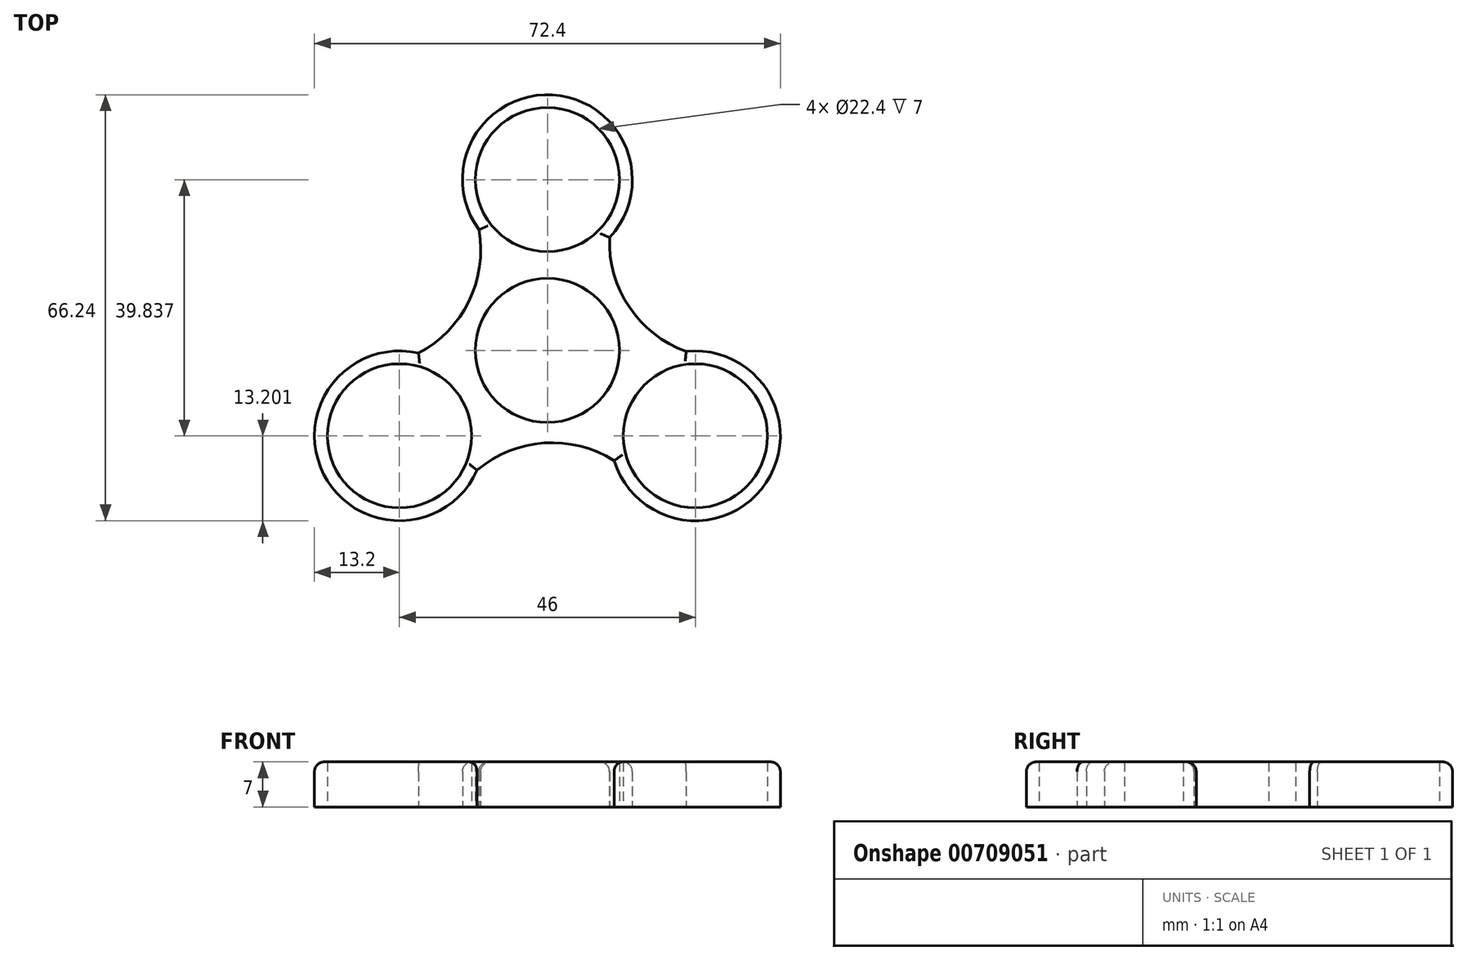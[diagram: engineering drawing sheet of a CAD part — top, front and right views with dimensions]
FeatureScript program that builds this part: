
annotation { "Feature Type Name" : "Feature", "Feature Type Description" : "" }
export const myFeature = defineFeature(function(context is Context, id is Id, definition is map)
    precondition{}
    {
        {
            var Q0;
            Q0=qCreatedBy(makeId("Top.planeOp"),FACE);
            var sketch = newSketch(context, id + "F0", { "sketchPlane" : qUnion([Q0])});
            skCircle(sketch, "E0", {"center": v(0, 0) * mm, "radius": 11.2 * mm});
            skCircle(sketch, "E1", {"center": v(0, 26.56) * mm, "radius": 11.2 * mm});
            skArc(sketch, "E2", {"start": v(9.66, 17.56) * mm, "mid": v(0.78, 39.74) * mm, "end": v(-10.65, 18.76) * mm});
            skArc(sketch, "E3.1.0", {"start": v(-20.04, -0.42) * mm, "mid": v(-34.8, -19.2) * mm, "end": v(-10.92, -18.6) * mm});
            skCircle(sketch, "E3.1.1", {"center": v(-23, -13.28) * mm, "radius": 11.2 * mm});
            skArc(sketch, "E3.2.0", {"start": v(10.38, -17.15) * mm, "mid": v(34.02, -20.54) * mm, "end": v(21.57, -0.16) * mm});
            skCircle(sketch, "E3.2.1", {"center": v(23, -13.28) * mm, "radius": 11.2 * mm});
            skArc(sketch, "E4", {"start": v(9.66, 17.56) * mm, "mid": v(12.72, 6.75) * mm, "end": v(21.57, -0.16) * mm});
            skArc(sketch, "E5.1.0", {"start": v(-20.04, -0.42) * mm, "mid": v(-12.2, 7.64) * mm, "end": v(-10.65, 18.76) * mm});
            skArc(sketch, "E5.2.0", {"start": v(10.38, -17.15) * mm, "mid": v(-0.51, -14.39) * mm, "end": v(-10.92, -18.6) * mm});
            skSolve(sketch);
        }
        {
            var Q0;
            Q0=makeQuery(id+"F0.imprint","IMPRINT",FACE,{"disambiguationData":[TD([[makeQuery(id+"F0.imprint","IMPRINT",EDGE,{"derivedFrom":sQuery(id+"F0.wireOp",EDGE,"E0")}),-1.0]])]});
            extrude(context, id + "F1", {"entities" : qUnion([Q0]), "depth" : 7 * mm, "offsetDistance" : 25 * mm});
        }
        {
            var Q0;
            Q0=makeQuery(id+"F1.opExtrude","CAP_EDGE",EDGE,{"disambiguationData":[OSD([sQuery(id+"F0.wireOp",EDGE,"E5.2.0")])],"isStart":false});
            var Q1;
            Q1=makeQuery(id+"F1.opExtrude","CAP_EDGE",EDGE,{"disambiguationData":[OSD([sQuery(id+"F0.wireOp",EDGE,"E3.1.0")])],"isStart":false});
            var Q2;
            Q2=makeQuery(id+"F1.opExtrude","CAP_EDGE",EDGE,{"disambiguationData":[OSD([sQuery(id+"F0.wireOp",EDGE,"E5.1.0")])],"isStart":false});
            var Q3;
            Q3=makeQuery(id+"F1.opExtrude","CAP_EDGE",EDGE,{"disambiguationData":[OSD([sQuery(id+"F0.wireOp",EDGE,"E2")])],"isStart":false});
            var Q4;
            Q4=makeQuery(id+"F1.opExtrude","CAP_EDGE",EDGE,{"disambiguationData":[OSD([sQuery(id+"F0.wireOp",EDGE,"E4")])],"isStart":false});
            var Q5;
            Q5=makeQuery(id+"F1.opExtrude","CAP_EDGE",EDGE,{"disambiguationData":[OSD([sQuery(id+"F0.wireOp",EDGE,"E3.2.0")])],"isStart":false});
            fillet(context, id + "F2", {"entities" : qUnion([Q0, Q1, Q2, Q3, Q4, Q5]), "radius" : 1.5 * mm, "tangentPropagation" : true, "allowEdgeOverflow" : false});
        }
    });
